# Revit family: Seat-LaZBoy-Koncert_Behavioral_Health-KOT19
name_source: partatom
category: Furniture
revit_build: Autodesk Revit 2017 (Build: 20160225_1515(x64)
units: mm (PartAtom-declared; Revit-internal decimal feet)

## family parameters
Always vertical = Yes
Cut with Voids When Loaded = No
OmniClass Number = 23.40.20.00
Room Calculation Point = No
Shared = No
Work Plane-Based = No

## types (4) — shared parameters
Assembly Code = E2020200
Depth = 29.50"
Height = 33.25"
Manufacturer = LaZBoy
Product Documentation Link = URL
URL = URL
Width = 24.30"

## per-type parameters (varying)
| type | Description | Model |
| Urethane Armcaps | Behavioral Health Chair with Urethane Arm Caps | KOT19U |
| Wood Armcaps | Behavioral Health Chair with Wood Arm Caps | KOT19W |
| Wood Arm Caps | Behavioral Health Chair with Wood Arm Caps | KOT19W |
| Urethane Arm Cps | Behavioral Health Chair with Urethane Arm Caps | KOT19U |

## geometry (parser evidence)
native form markers: Sweep x8
no freeform markers — native parametric forms only
